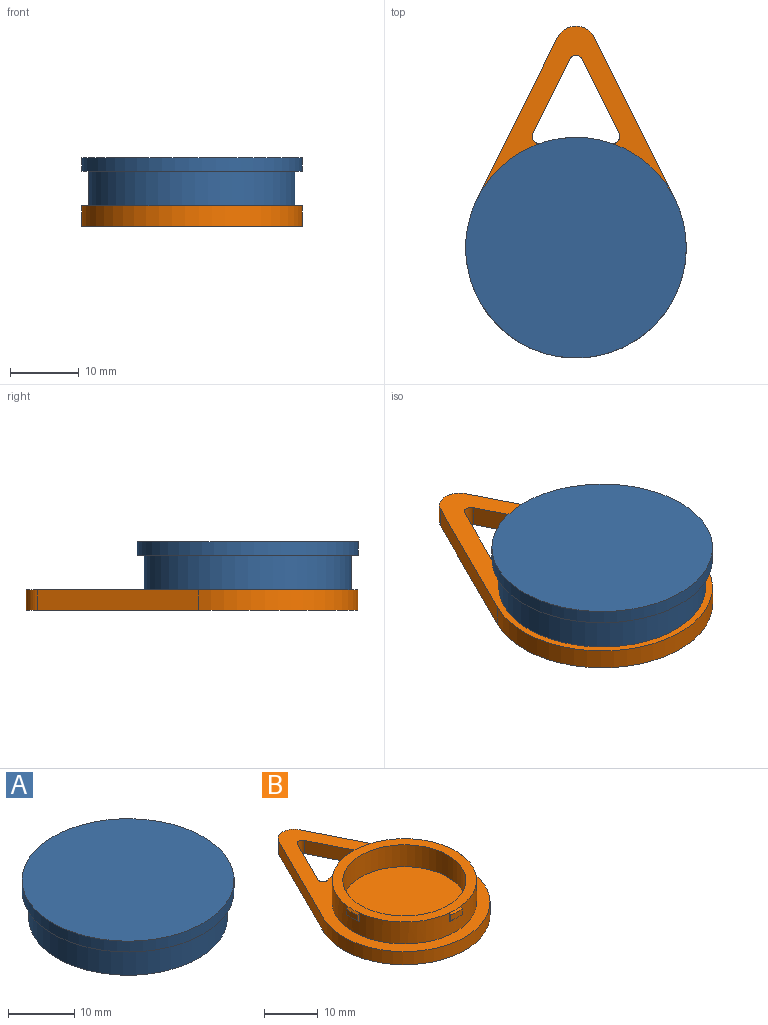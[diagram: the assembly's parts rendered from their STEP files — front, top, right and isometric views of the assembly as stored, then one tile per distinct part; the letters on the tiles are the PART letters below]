
ASSEMBLY  parts=2 mates=1
PART A: 10 faces, bbox 32x32x7 mm
  f0: cylinder r=16mm len=32mm, axis (0,0,-1), area 201.1mm2, adj f1,f3
  f1: plane 32x32mm, normal (0,0,1), area 804.2mm2, adj f0
  f2: cylinder r=15mm len=30mm, axis (0,0,-1), area 471.2mm2, adj f3,f4
  f3: plane 32x32mm, normal (0,0,-1), area 97.4mm2, adj f0,f2
  f4: plane 30x30mm, normal (0,0,-1), area 82.3mm2, adj f2,f8
  f5: cylinder r=13.7mm len=27.4mm, axis (0,0,-1), area 206.6mm2, adj f8,f9
  f6: plane 28.2x28.2mm, normal (0,0,-1), area 624.6mm2, adj f7
  f7: cylinder r=14.1mm len=28.2mm, axis (0,0,-1), area 159.5mm2, adj f6,f9
  f8: cone r=13.7mm half-angle=45deg, axis (0,0,-1), area 49.4mm2, adj f4,f5
  f9: cone r=13.7mm half-angle=45deg, axis (0,0,1), area 49.4mm2, adj f5,f7
PART B: 36 faces, bbox 32x48.1x8 mm
  f0: cylinder r=13.5mm len=27mm, axis (0,0,-1), area 400.1mm2, adj f8,f11,f13,f14,f16,f17,f19,f20
  f1: plane 23.35x11.64mm, normal (-0.9,0.45,0), area 78.3mm2, adj f2,f7,f8,f9
  f2: cylinder r=16mm len=32mm, axis (0,0,-1), area 195.2mm2, adj f1,f3,f8,f9
  f3: plane 23.35x11.64mm, normal (0.9,0.45,0), area 78.3mm2, adj f2,f7,f8,f9
  f4: cylinder r=16mm len=10.11mm, axis (0,0,-1), area 30.8mm2, adj f8,f9,f33,f35
  f5: plane 10.77x5.37mm, normal (0.9,-0.45,0), area 36.1mm2, adj f8,f9,f33,f34
  f6: plane 10.77x5.37mm, normal (-0.9,-0.45,0), area 36.1mm2, adj f8,f9,f34,f35
  f7: cylinder r=3mm len=5.37mm, axis (0,0,-1), area 20mm2, adj f1,f3,f8,f9
  f8: plane 48.15x32mm, normal (0,0,1), area 363.8mm2, adj f0,f1,f2,f3,f4,f5,f6,f7
  f9: plane 48.15x32mm, normal (0,0,-1), area 936.4mm2, adj f1,f2,f3,f4,f5,f6,f7,f33
  f10: cylinder r=11.5mm len=23mm, axis (0,0,-1), area 361.3mm2, adj f11,f12
  f11: plane 27x27mm, normal (0,0,1), area 157.1mm2, adj f0,f10,f25,f27,f29,f31
  f12: plane 23x23mm, normal (0,0,1), area 415.5mm2, adj f10
  f13: plane 2x0.38mm, normal (-1,0,0), area 0.6mm2, adj f0,f15,f31,f32
  f14: plane 2x0.38mm, normal (1,0,0), area 0.6mm2, adj f0,f15,f31,f32
  f15: cylinder r=13.88mm len=3mm, axis (0,0,1), area 3.7mm2, adj f13,f14,f31,f32
  f16: plane 2x0.38mm, normal (0,-1,0), area 0.6mm2, adj f0,f18,f25,f26
  f17: plane 2x0.38mm, normal (0,1,0), area 0.6mm2, adj f0,f18,f25,f26
  f18: cylinder r=13.88mm len=3mm, axis (0,0,1), area 3.7mm2, adj f16,f17,f25,f26
  f19: plane 2x0.38mm, normal (1,0,0), area 0.6mm2, adj f0,f21,f27,f28
  f20: plane 2x0.38mm, normal (-1,0,0), area 0.6mm2, adj f0,f21,f27,f28
  f21: cylinder r=13.88mm len=3mm, axis (0,0,1), area 3.7mm2, adj f19,f20,f27,f28
  f22: plane 2x0.38mm, normal (0,1,0), area 0.6mm2, adj f0,f24,f29,f30
  f23: plane 2x0.38mm, normal (0,-1,0), area 0.6mm2, adj f0,f24,f29,f30
  f24: cylinder r=13.88mm len=3mm, axis (0,0,1), area 3.7mm2, adj f22,f23,f29,f30
  f25: cone r=13.5mm half-angle=45deg, axis (0,0,-1), area 1.6mm2, adj f11,f16,f17,f18
  f26: cone r=13.88mm half-angle=45deg, axis (0,0,1), area 1.6mm2, adj f0,f16,f17,f18
  f27: cone r=13.5mm half-angle=45deg, axis (0,0,-1), area 1.6mm2, adj f11,f19,f20,f21
  f28: cone r=13.88mm half-angle=45deg, axis (0,0,1), area 1.6mm2, adj f0,f19,f20,f21
  f29: cone r=13.5mm half-angle=45deg, axis (0,0,-1), area 1.6mm2, adj f11,f22,f23,f24
  f30: cone r=13.88mm half-angle=45deg, axis (0,0,1), area 1.6mm2, adj f0,f22,f23,f24
  f31: cone r=13.5mm half-angle=45deg, axis (0,0,-1), area 1.6mm2, adj f11,f13,f14,f15
  f32: cone r=13.88mm half-angle=45deg, axis (0,0,1), area 1.6mm2, adj f0,f13,f14,f15
  f33: cylinder r=1mm len=3mm, axis (0,0,-1), area 7.1mm2, adj f4,f5,f8,f9
  f34: cylinder r=1mm len=3mm, axis (0,0,1), area 6.7mm2, adj f5,f6,f8,f9
  f35: cylinder r=1mm len=3mm, axis (0,0,-1), area 7.1mm2, adj f4,f6,f8,f9
PLACE A t=(36.32,18.73,-4.41)mm
PLACE B t=(36.32,18.73,-7.41)mm
MATE fastened B.f10 <-> A.f0  axis (0,0,1) through (36.32,18.73,-4.41)mm
